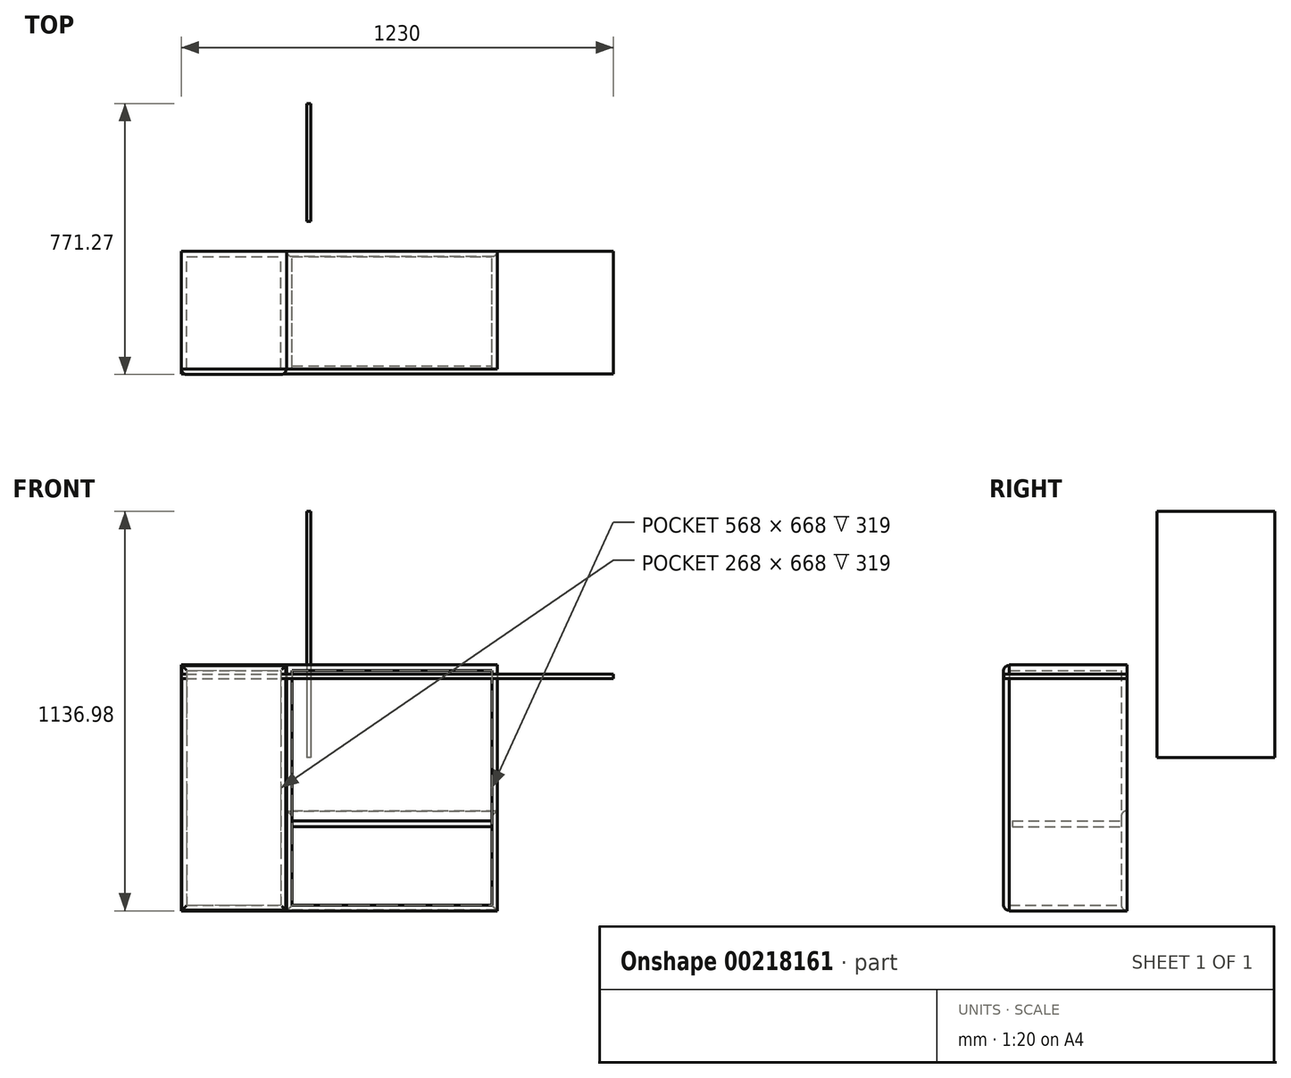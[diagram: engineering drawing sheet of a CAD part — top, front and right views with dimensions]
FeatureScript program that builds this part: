
annotation { "Feature Type Name" : "Feature", "Feature Type Description" : "" }
export const myFeature = defineFeature(function(context is Context, id is Id, definition is map)
    precondition{}
    {
        {
            var Q0;
            Q0=qCreatedBy(makeId("Front.planeOp"),FACE);
            var sketch = newSketch(context, id + "F0", { "sketchPlane" : qUnion([Q0])});
            skLineSegment(sketch, "E0.bottom", {"start": v(-357.2, 38.32) * mm, "end": v(-57.2, 38.32) * mm});
            skLineSegment(sketch, "E0.top", {"start": v(-357.2, -661.68) * mm, "end": v(-57.2, -661.68) * mm});
            skLineSegment(sketch, "E0.left", {"start": v(-357.2, 38.32) * mm, "end": v(-357.2, -661.68) * mm});
            skLineSegment(sketch, "E0.right", {"start": v(-57.2, 38.32) * mm, "end": v(-57.2, -661.68) * mm});
            skSolve(sketch);
        }
        {
            var Q0;
            Q0 = qSketchRegion(id + "F0", true);
            extrude(context, id + "F1", {"entities" : qUnion([Q0]), "depth" : 335 * mm});
        }
        {
            var Q0;
            Q0=makeQuery(id+"F1.opExtrude","CAP_FACE",FACE,{"disambiguationData":[OSD([sQuery(id+"F0.wireOp",EDGE,"E0.bottom"),sQuery(id+"F0.wireOp",EDGE,"E0.top"),sQuery(id+"F0.wireOp",EDGE,"E0.left"),sQuery(id+"F0.wireOp",EDGE,"E0.right")])],"isStart":false});
            shell(context, id + "F2", {"entities" : qUnion([Q0]), "thickness" : 16 * mm});
        }
        {
            var Q0;
            Q0=qCreatedBy(makeId("Front.planeOp"),FACE);
            var sketch = newSketch(context, id + "F3", { "sketchPlane" : qUnion([Q0])});
            skLineSegment(sketch, "E1.0", {"start": v(-57.2, 38.32) * mm, "end": v(-57.2, -661.68) * mm});
            skLineSegment(sketch, "E2.bottom", {"start": v(-57.2, 38.32) * mm, "end": v(542.8, 38.32) * mm});
            skLineSegment(sketch, "E2.top", {"start": v(-57.2, -661.68) * mm, "end": v(542.8, -661.68) * mm});
            skLineSegment(sketch, "E2.right", {"start": v(542.8, 38.32) * mm, "end": v(542.8, -661.68) * mm});
            skSolve(sketch);
        }
        {
            var Q0;
            Q0 = qSketchRegion(id + "F3", true);
            extrude(context, id + "F4", {"entities" : qUnion([Q0]), "depth" : 335 * mm});
        }
        {
            var Q0;
            Q0=makeQuery(id+"F4.opExtrude","CAP_FACE",FACE,{"disambiguationData":[OSD([sQuery(id+"F3.wireOp",EDGE,"E2.bottom"),sQuery(id+"F3.wireOp",EDGE,"E2.top"),sQuery(id+"F3.wireOp",EDGE,"E1.0"),sQuery(id+"F3.wireOp",EDGE,"E2.right")])],"isStart":false});
            shell(context, id + "F5", {"entities" : qUnion([Q0]), "thickness" : 16 * mm});
        }
        {
            var Q0;
            Q0=makeQuery(id+"F5.opShell","OFFSET_FACE",FACE,{"disambiguationData":[OSD([sQuery(id+"F3.wireOp",EDGE,"E2.bottom"),sQuery(id+"F3.wireOp",EDGE,"E2.top"),sQuery(id+"F3.wireOp",EDGE,"E1.0"),sQuery(id+"F3.wireOp",EDGE,"E2.right")])]});
            var sketch = newSketch(context, id + "F6", { "sketchPlane" : qUnion([Q0])});
            skLineSegment(sketch, "E3.bottom", {"start": v(-41.2, -405.81) * mm, "end": v(526.8, -405.81) * mm});
            skLineSegment(sketch, "E3.top", {"start": v(-41.2, -421.81) * mm, "end": v(526.8, -421.81) * mm});
            skLineSegment(sketch, "E3.left", {"start": v(-41.2, -405.81) * mm, "end": v(-41.2, -421.81) * mm});
            skLineSegment(sketch, "E3.right", {"start": v(526.8, -405.81) * mm, "end": v(526.8, -421.81) * mm});
            skSolve(sketch);
        }
        {
            var Q0;
            Q0 = qSketchRegion(id + "F6", true);
            extrude(context, id + "F7", {"entities" : qUnion([Q0]), "depth" : 310 * mm});
        }
        {
            var Q0;
            Q0=makeQuery(id+"F1.opExtrude","CAP_FACE",FACE,{"disambiguationData":[OSD([sQuery(id+"F0.wireOp",EDGE,"E0.bottom"),sQuery(id+"F0.wireOp",EDGE,"E0.top"),sQuery(id+"F0.wireOp",EDGE,"E0.left"),sQuery(id+"F0.wireOp",EDGE,"E0.right")])],"isStart":false});
            var sketch = newSketch(context, id + "F8", { "sketchPlane" : qUnion([Q0])});
            skPoint(sketch, "E4.0", {"position": v(-357.2, 38.32) * mm});
            skPoint(sketch, "E5.0", {"position": v(-57.2, -661.68) * mm});
            skLineSegment(sketch, "E6.bottom", {"start": v(-355.2, 36.32) * mm, "end": v(-59.2, 36.32) * mm});
            skLineSegment(sketch, "E6.top", {"start": v(-355.2, -659.68) * mm, "end": v(-59.2, -659.68) * mm});
            skLineSegment(sketch, "E6.left", {"start": v(-355.2, 36.32) * mm, "end": v(-355.2, -659.68) * mm});
            skLineSegment(sketch, "E6.right", {"start": v(-59.2, 36.32) * mm, "end": v(-59.2, -659.68) * mm});
            skSolve(sketch);
        }
        {
            var Q0;
            Q0 = qSketchRegion(id + "F8", true);
            extrude(context, id + "F9", {"entities" : qUnion([Q0]), "depth" : 16 * mm});
        }
        {
            var Q0;
            Q0=qCreatedBy(makeId("Right.planeOp"),FACE);
            var sketch = newSketch(context, id + "F10", { "sketchPlane" : qUnion([Q0])});
            skLineSegment(sketch, "E7.bottom", {"start": v(85.27, 475.3) * mm, "end": v(420.27, 475.3) * mm});
            skLineSegment(sketch, "E7.top", {"start": v(85.27, -224.7) * mm, "end": v(420.27, -224.7) * mm});
            skLineSegment(sketch, "E7.left", {"start": v(85.27, 475.3) * mm, "end": v(85.27, -224.7) * mm});
            skLineSegment(sketch, "E7.right", {"start": v(420.27, 475.3) * mm, "end": v(420.27, -224.7) * mm});
            skSolve(sketch);
        }
        {
            var Q0;
            Q0 = qSketchRegion(id + "F10", true);
            extrude(context, id + "F11", {"entities" : qUnion([Q0]), "depth" : 12 * mm});
        }
        {
            var Q0;
            Q0=qCreatedBy(makeId("Top.planeOp"),FACE);
            var sketch = newSketch(context, id + "F12", { "sketchPlane" : qUnion([Q0])});
            skPoint(sketch, "E8.0", {"position": v(-357.2, 0) * mm});
            skLineSegment(sketch, "E9.bottom", {"start": v(-357.2, 0) * mm, "end": v(872.8, 0) * mm});
            skLineSegment(sketch, "E9.top", {"start": v(-357.2, -350) * mm, "end": v(872.8, -350) * mm});
            skLineSegment(sketch, "E9.left", {"start": v(-357.2, 0) * mm, "end": v(-357.2, -350) * mm});
            skLineSegment(sketch, "E9.right", {"start": v(872.8, 0) * mm, "end": v(872.8, -350) * mm});
            skSolve(sketch);
        }
        {
            var Q0;
            Q0 = qSketchRegion(id + "F12", true);
            extrude(context, id + "F13", {"entities" : qUnion([Q0]), "depth" : 12 * mm});
        }
        {
            var Q0;
            Q0=makeQuery(id+"F9.opExtrude","CAP_FACE",FACE,{"disambiguationData":[OSD([sQuery(id+"F8.wireOp",EDGE,"E6.bottom"),sQuery(id+"F8.wireOp",EDGE,"E6.top"),sQuery(id+"F8.wireOp",EDGE,"E6.left"),sQuery(id+"F8.wireOp",EDGE,"E6.right")])],"isStart":false});
            fillet(context, id + "F14", {"entities" : qUnion([Q0]), "radius" : 12 * mm, "tangentPropagation" : true, "rho" : 0.3, "crossSection" : FilletCrossSection.CONIC, "allowEdgeOverflow" : false});
        }
        {
            var Q0;
            Q0=qCreatedBy(makeId("Front.planeOp"),FACE);
            var sketch = newSketch(context, id + "F15", { "sketchPlane" : qUnion([Q0])});
            skPoint(sketch, "E10.0", {"position": v(542.8, -661.68) * mm});
            skPoint(sketch, "E11.0", {"position": v(-57.2, -661.68) * mm});
            skLineSegment(sketch, "E12.bottom", {"start": v(540.8, -659.68) * mm, "end": v(-55.2, -659.68) * mm});
            skLineSegment(sketch, "E12.top", {"start": v(540.8, -377.68) * mm, "end": v(-55.2, -377.68) * mm});
            skLineSegment(sketch, "E12.left", {"start": v(540.8, -659.68) * mm, "end": v(540.8, -377.68) * mm});
            skLineSegment(sketch, "E12.right", {"start": v(-55.2, -659.68) * mm, "end": v(-55.2, -377.68) * mm});
            skSolve(sketch);
        }
        {
            var Q0;
            Q0 = qSketchRegion(id + "F15", true);
            extrude(context, id + "F16", {"entities" : qUnion([Q0]), "depth" : 16 * mm});
        }
        {
            var Q0;
            Q0=makeQuery(id+"F16.opExtrude","CAP_FACE",FACE,{"disambiguationData":[OSD([sQuery(id+"F15.wireOp",EDGE,"E12.bottom"),sQuery(id+"F15.wireOp",EDGE,"E12.top"),sQuery(id+"F15.wireOp",EDGE,"E12.left"),sQuery(id+"F15.wireOp",EDGE,"E12.right")])],"isStart":false});
            fillet(context, id + "F17", {"entities" : qUnion([Q0]), "radius" : 12 * mm, "tangentPropagation" : true, "rho" : 0.3, "crossSection" : FilletCrossSection.CONIC, "allowEdgeOverflow" : false});
        }
    });
